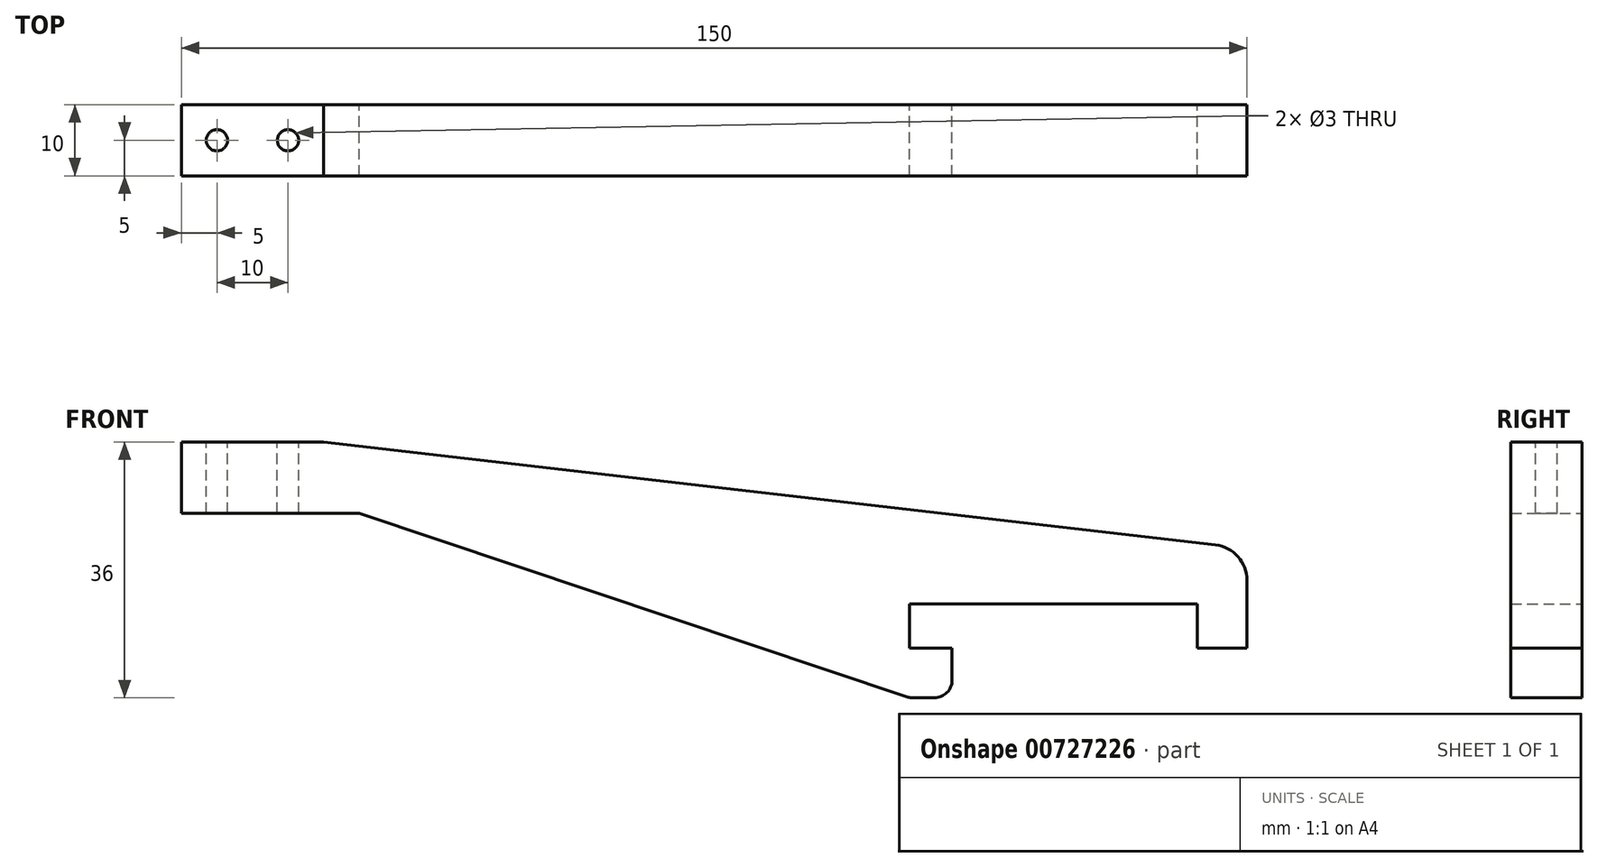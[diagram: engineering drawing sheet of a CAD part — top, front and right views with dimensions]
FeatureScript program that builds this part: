
annotation { "Feature Type Name" : "Feature", "Feature Type Description" : "" }
export const myFeature = defineFeature(function(context is Context, id is Id, definition is map)
    precondition{}
    {
        {
            var Q0;
            Q0=qCreatedBy(makeId("Front.planeOp"),FACE);
            var sketch = newSketch(context, id + "F0", { "sketchPlane" : qUnion([Q0])});
            skLineSegment(sketch, "E0.bottom", {"start": v(0, 0) * mm, "end": v(-40.5, 0) * mm});
            skLineSegment(sketch, "E0.top", {"start": v(-34.5, -6.2) * mm, "end": v(-40.5, -6.2) * mm});
            skLineSegment(sketch, "E0.left", {"start": v(0, 0) * mm, "end": v(0, -6.2) * mm});
            skLineSegment(sketch, "E0.right", {"start": v(-40.5, 0) * mm, "end": v(-40.5, -6.2) * mm});
            skLineSegment(sketch, "E1", {"start": v(0, -6.2) * mm, "end": v(7, -6.2) * mm});
            skLineSegment(sketch, "E2", {"start": v(7, -6.2) * mm, "end": v(7, 7.8) * mm});
            skLineSegment(sketch, "E3", {"start": v(7, 7.8) * mm, "end": v(-123, 22.8) * mm});
            skLineSegment(sketch, "E4", {"start": v(-40.5, -6.2) * mm, "end": v(-34.5, -6.2) * mm});
            skLineSegment(sketch, "E5", {"start": v(-34.5, -6.2) * mm, "end": v(-34.5, -13.2) * mm});
            skLineSegment(sketch, "E6", {"start": v(-34.5, -13.2) * mm, "end": v(-40.5, -13.2) * mm});
            skLineSegment(sketch, "E7", {"start": v(-123, 22.8) * mm, "end": v(-143, 22.8) * mm});
            skLineSegment(sketch, "E8", {"start": v(-143, 22.8) * mm, "end": v(-143, 12.8) * mm});
            skLineSegment(sketch, "E9", {"start": v(-143, 12.8) * mm, "end": v(-118, 12.8) * mm});
            skLineSegment(sketch, "E10", {"start": v(-118, 12.8) * mm, "end": v(-40.5, -13.2) * mm});
            skSolve(sketch);
        }
        {
            var Q0;
            Q0=makeQuery(id+"F0.imprint","IMPRINT",FACE,{"disambiguationData":[TD([[makeQuery(id+"F0.imprint","IMPRINT",EDGE,{"derivedFrom":sQuery(id+"F0.wireOp",EDGE,"E0.bottom")}),-1.0]])]});
            extrude(context, id + "F1", {"entities" : qUnion([Q0]), "depth" : 10 * mm, "offsetDistance" : 25 * mm});
        }
        {
            var Q0;
            Q0=makeQuery(id+"F1.opExtrude","SWEPT_EDGE",EDGE,{"disambiguationData":[OSD([sQuery(id+"F0.wireOp",EDGE,"E2"),sQuery(id+"F0.wireOp",EDGE,"E3")])]});
            fillet(context, id + "F2", {"entities" : qUnion([Q0]), "radius" : 5 * mm, "tangentPropagation" : true, "allowEdgeOverflow" : false});
        }
        {
            var Q0;
            Q0=makeQuery(id+"F1.opExtrude","SWEPT_EDGE",EDGE,{"disambiguationData":[OSD([sQuery(id+"F0.wireOp",EDGE,"E5"),sQuery(id+"F0.wireOp",EDGE,"E6")])]});
            var Q1;
            Q1=makeQuery(id+"F1.opExtrude","SWEPT_EDGE",EDGE,{"disambiguationData":[OSD([sQuery(id+"F0.wireOp",EDGE,"E6"),sQuery(id+"F0.wireOp",EDGE,"E10")])]});
            fillet(context, id + "F3", {"entities" : qUnion([Q0, Q1]), "radius" : 2.5 * mm, "tangentPropagation" : true, "allowEdgeOverflow" : false});
        }
        {
            var Q0;
            Q0=makeQuery(id+"F1.opExtrude","SWEPT_FACE",FACE,{"disambiguationData":[OSD([sQuery(id+"F0.wireOp",EDGE,"E7")])]});
            var sketch = newSketch(context, id + "F4", { "sketchPlane" : qUnion([Q0])});
            skCircle(sketch, "E11", {"center": v(-138, -5) * mm, "radius": 1.5 * mm});
            skCircle(sketch, "E12", {"center": v(-128, -5) * mm, "radius": 1.5 * mm});
            skSolve(sketch);
        }
        {
            var Q0;
            Q0=makeQuery(id+"F4.imprint","IMPRINT",FACE,{"disambiguationData":[TD([[makeQuery(id+"F4.imprint","IMPRINT",EDGE,{"derivedFrom":sQuery(id+"F4.wireOp",EDGE,"E12")}),1.0]])]});
            var Q1;
            Q1=makeQuery(id+"F4.imprint","IMPRINT",FACE,{"disambiguationData":[TD([[makeQuery(id+"F4.imprint","IMPRINT",EDGE,{"derivedFrom":sQuery(id+"F4.wireOp",EDGE,"E11")}),1.0]])]});
            extrude(context, id + "F5", {"entities" : qUnion([Q0, Q1]), "operationType" : NewBodyOperationType.REMOVE, "oppositeDirection" : true, "depth" : 25 * mm, "offsetDistance" : 25 * mm});
        }
    });
